# Revit family: Toilet_Tank-In_Wall-KOHLER-HYDRO_TOWER-K-20010T_1
name_source: partatom
category: Plumbing Fixtures
revit_build: Autodesk Revit 2017 (Build: 20160225_1515(x64)
units: mm (PartAtom-declared; Revit-internal decimal feet)

## family parameters
Cut with Voids When Loaded = No
Host = Face
OmniClass Number = 23.31.19.19.19
OmniClass Title = Water Closet Tanks
Part Type = Normal
Room Calculation Point = No
Round Connector Dimension = Use Diameter
Shared = No

## types (1)
- NA-Stainless Steel
    ADA Compliant = No
    Assembly Code = D2010100
    CW Connection = Yes
    Cold Water Inlet = Cold Water Inlet
    Cold Water Outlet = Cold Water Outlet
    Date Modified = 01/06/2021
    Default Elevation = 0"
    Description = 300 PNE In Wall Tank 3/4.5 L
    Finish = Kohler-Metal-NA-Stainless
    Flow Rate = 0 GPM
    Flush Rate- GPF = 0 GPF
    Flush Rate- LPF = 0 LPF
    HW Connection = No
    Hot Water Inlet = Hot Water Inlet
    Length = 4 1/4"
    Manufacturer = KOHLER Co.
    Master Format 2014 = 22 42 13.13
    Master Format 2014 Name = Residential Water Closets
    Material = Premium Metal Construction
    Model = K-20010T-PNE-NA
    Pressure = 0.00 psi
    Product Name = HYDRO_TOWER
    Seat Included = No
    Type = 1
    URL = http://www.kohler.com.cn
    Vent Connection = No
    Waste Connection = Yes
    Waste Water Inlet = Waste Water Inlet
    Waste Water Outlet = Waste Water Outlet
    WaterSense Certified = No
    Width = 18 13/16"

## geometry (parser evidence)
native form markers: Sweep x4
no freeform markers — native parametric forms only
